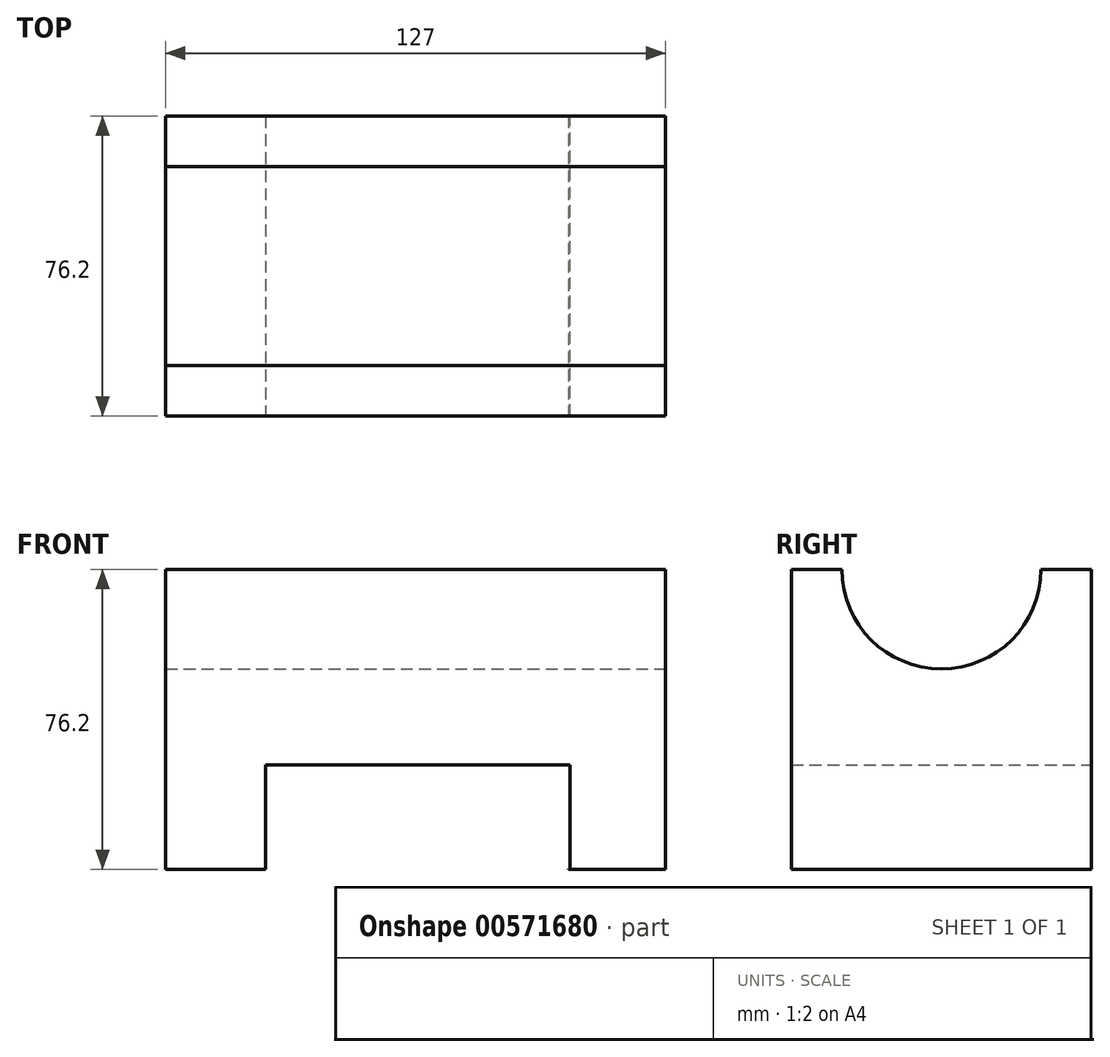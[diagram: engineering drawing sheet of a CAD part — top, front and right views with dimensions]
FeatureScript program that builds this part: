
annotation { "Feature Type Name" : "Feature", "Feature Type Description" : "" }
export const myFeature = defineFeature(function(context is Context, id is Id, definition is map)
    precondition{}
    {
        {
            var Q0;
            Q0=qCreatedBy(makeId("Front.planeOp"),FACE);
            var sketch = newSketch(context, id + "F0", { "sketchPlane" : qUnion([Q0])});
            skLineSegment(sketch, "E0", {"start": v(-57.68, -10.23) * mm, "end": v(69.32, -10.23) * mm});
            skLineSegment(sketch, "E1", {"start": v(-57.68, -10.23) * mm, "end": v(-57.68, 65.97) * mm});
            skLineSegment(sketch, "E2", {"start": v(69.32, -10.23) * mm, "end": v(69.32, 65.97) * mm});
            skLineSegment(sketch, "E3", {"start": v(-57.68, 65.97) * mm, "end": v(69.32, 65.97) * mm});
            skSolve(sketch);
        }
        {
            var Q0;
            Q0=qCreatedBy(makeId("Top.planeOp"),FACE);
            var sketch = newSketch(context, id + "F1", { "sketchPlane" : qUnion([Q0])});
            skSolve(sketch);
        }
        {
            var Q0;
            Q0 = qSketchRegion(id + "F1", true);
            var Q1;
            Q1=makeQuery(id+"F0.imprint","IMPRINT",FACE,{"disambiguationData":[TD([[makeQuery(id+"F0.imprint","IMPRINT",EDGE,{"derivedFrom":sQuery(id+"F0.wireOp",EDGE,"E0")}),1.0]])]});
            extrude(context, id + "F2", {"entities" : qUnion([Q0, Q1]), "depth" : 76.2 * mm, "offsetDistance" : 25.4 * mm});
        }
        {
            var Q0;
            Q0=qCreatedBy(makeId("Front.planeOp"),FACE);
            var sketch = newSketch(context, id + "F3", { "sketchPlane" : qUnion([Q0])});
            skLineSegment(sketch, "E4.bottom", {"start": v(-32.34, -10.05) * mm, "end": v(45.01, -10.05) * mm});
            skLineSegment(sketch, "E4.top", {"start": v(-32.34, 16.37) * mm, "end": v(45.01, 16.37) * mm});
            skLineSegment(sketch, "E4.left", {"start": v(-32.34, -10.05) * mm, "end": v(-32.34, 16.37) * mm});
            skLineSegment(sketch, "E4.right", {"start": v(45.01, -10.05) * mm, "end": v(45.01, 16.37) * mm});
            skPoint(sketch, "E5.end.orphan", {"position": v(45.01, -10.05) * mm});
            skPoint(sketch, "E5.start.orphan", {"position": v(70.41, -10.05) * mm});
            skSolve(sketch);
        }
        {
            var Q0;
            Q0 = qSketchRegion(id + "F3", true);
            extrude(context, id + "F4", {"entities" : qUnion([Q0]), "operationType" : NewBodyOperationType.REMOVE, "depth" : 88.14 * mm, "offsetDistance" : 25.4 * mm});
        }
        {
            var Q0;
            Q0=makeQuery(id+"F2.opExtrude","CAP_FACE",FACE,{"disambiguationData":[OSD([sQuery(id+"F0.wireOp",EDGE,"E0"),sQuery(id+"F0.wireOp",EDGE,"E1"),sQuery(id+"F0.wireOp",EDGE,"E2"),sQuery(id+"F0.wireOp",EDGE,"E3")])],"isStart":false});
            var sketch = newSketch(context, id + "F5", { "sketchPlane" : qUnion([Q0])});
            skLineSegment(sketch, "E6.bottom", {"start": v(-32.34, -10.05) * mm, "end": v(44.64, -10.05) * mm});
            skLineSegment(sketch, "E6.top", {"start": v(-32.34, -17.4) * mm, "end": v(44.64, -17.4) * mm});
            skLineSegment(sketch, "E6.left", {"start": v(-32.34, -10.05) * mm, "end": v(-32.34, -17.4) * mm});
            skLineSegment(sketch, "E6.right", {"start": v(44.64, -10.05) * mm, "end": v(44.64, -17.4) * mm});
            skSolve(sketch);
        }
        {
            var Q0;
            Q0 = qSketchRegion(id + "F5", true);
            extrude(context, id + "F6", {"entities" : qUnion([Q0]), "operationType" : NewBodyOperationType.REMOVE, "oppositeDirection" : true, "depth" : 93.98 * mm, "offsetDistance" : 25.4 * mm});
        }
        {
            var Q0;
            Q0=makeQuery(id+"F2.opExtrude","SWEPT_FACE",FACE,{"disambiguationData":[OSD([sQuery(id+"F0.wireOp",EDGE,"E2")])]});
            var sketch = newSketch(context, id + "F7", { "sketchPlane" : qUnion([Q0])});
            skLineSegment(sketch, "E7", {"start": v(-76.2, 65.97) * mm, "end": v(-63.5, 65.97) * mm});
            skLineSegment(sketch, "E8", {"start": v(0, 65.97) * mm, "end": v(-12.7, 65.97) * mm});
            skCircle(sketch, "E9", {"center": v(-38.1, 65.97) * mm, "radius": 25.28 * mm});
            skSolve(sketch);
        }
        {
            var Q0;
            Q0 = qSketchRegion(id + "F7", true);
            extrude(context, id + "F8", {"entities" : qUnion([Q0]), "operationType" : NewBodyOperationType.REMOVE, "oppositeDirection" : true, "depth" : 142.5 * mm, "offsetDistance" : 25.4 * mm});
        }
    });
